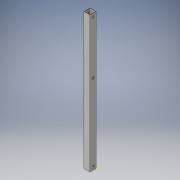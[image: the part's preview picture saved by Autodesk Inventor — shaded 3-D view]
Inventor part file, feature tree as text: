
AUTODESK INVENTOR PART (.ipt)
format: ipt  version: 2016 (Build 200138000, 138)  size: 139,264 bytes
history: native  units: in
note: dims shown in document units (in); Inventor stores cm internally (conversion verified against a paired STEP export)
features: sketch x5, extrude x4
ambient origin geometry x8: Origin, YZ Plane, XZ Plane, XY Plane, X Axis, Y Axis, Z Axis, Center Point
bodies: Solid1 (feature_tree)
feature tree (9):
  extrude  "Extrusion1"  Depth=1.0in
  extrude  "Extrusion2"  Depth=0.0625in
  extrude  "Extrusion3"  Depth=0.0625in
  sketch  "Sketch4"  dims[d6=21.6in d7=0.0in d9=0.5in]
  extrude  "Extrusion4"  Depth=21.6in
  sketch  "Sketch1"  dims[d0=1.0in d1=1.0in]
  sketch  "Sketch2"  dims[d2=0.0625in d3=0.0625in]
  sketch  "Sketch3"  dims[d4=0.0625in d5=0.0625in]
  sketch  "Sketch5"  dims[d10=0.4in d11=0.5in d12=1.0in d13=0.0in d14=0.5in d15=0.5in d16=0.4in d17=1.0in d18=0.0in d19=0.4in d20=0.5in d21=8.4in d22=1.0in d23=0.0in]
